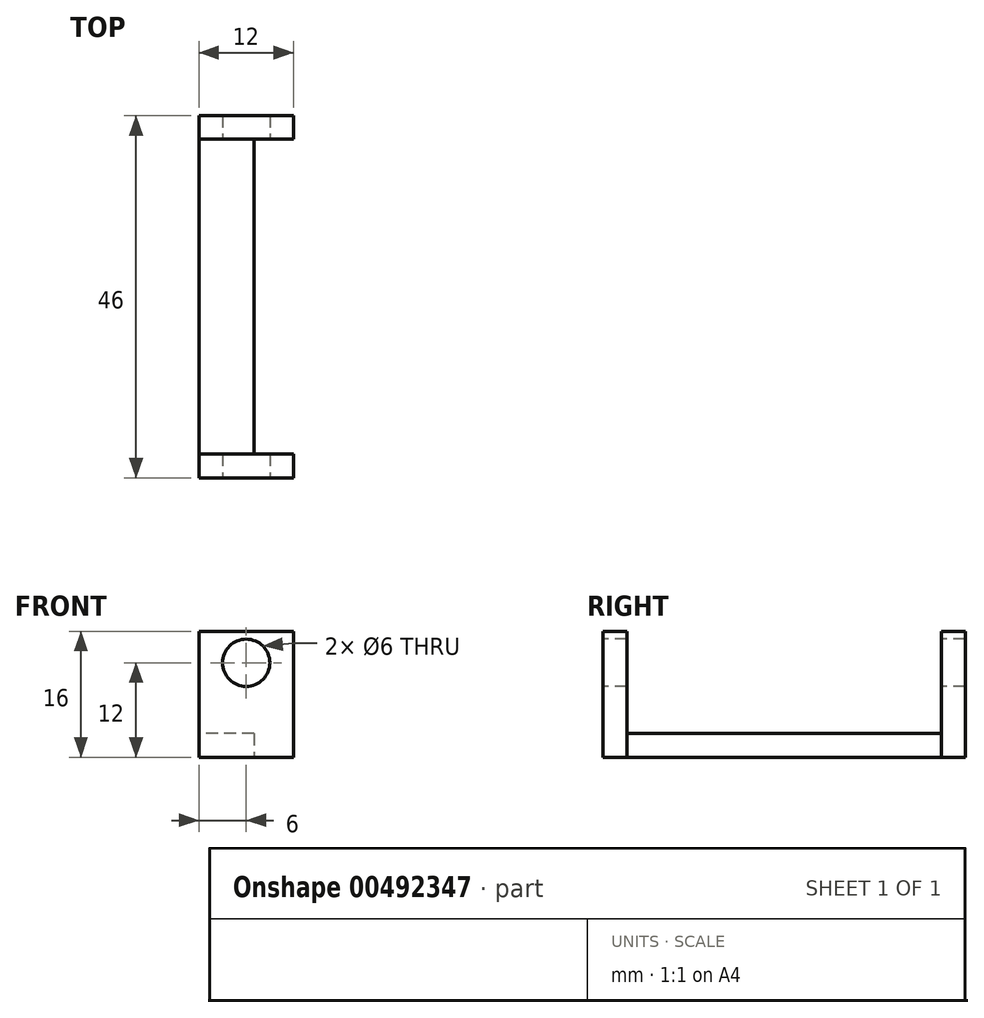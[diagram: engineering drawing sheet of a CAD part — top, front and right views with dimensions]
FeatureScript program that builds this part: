
annotation { "Feature Type Name" : "Feature", "Feature Type Description" : "" }
export const myFeature = defineFeature(function(context is Context, id is Id, definition is map)
    precondition{}
    {
        {
            var Q0;
            Q0=qCreatedBy(makeId("Top.planeOp"),FACE);
            var sketch = newSketch(context, id + "F0", { "sketchPlane" : qUnion([Q0])});
            skLineSegment(sketch, "E0.bottom", {"start": v(-1.5, 20) * mm, "end": v(1.5, 20) * mm});
            skLineSegment(sketch, "E0.top", {"start": v(-1.5, -20) * mm, "end": v(1.5, -20) * mm});
            skLineSegment(sketch, "E0.left", {"start": v(-1.5, 20) * mm, "end": v(-1.5, -20) * mm});
            skLineSegment(sketch, "E0.right", {"start": v(1.5, 20) * mm, "end": v(1.5, -20) * mm});
            skPoint(sketch, "E0.middle", {"position": v(0, 0) * mm});
            skLineSegment(sketch, "E1.bottom", {"start": v(-1.5, 20) * mm, "end": v(10.5, 20) * mm});
            skLineSegment(sketch, "E1.top", {"start": v(-1.5, 23) * mm, "end": v(10.5, 23) * mm});
            skLineSegment(sketch, "E1.left", {"start": v(-1.5, 20) * mm, "end": v(-1.5, 23) * mm});
            skLineSegment(sketch, "E1.right", {"start": v(10.5, 20) * mm, "end": v(10.5, 23) * mm});
            skLineSegment(sketch, "E2.bottom", {"start": v(-1.5, -20) * mm, "end": v(10.5, -20) * mm});
            skLineSegment(sketch, "E2.top", {"start": v(-1.5, -23) * mm, "end": v(10.5, -23) * mm});
            skLineSegment(sketch, "E2.left", {"start": v(-1.5, -20) * mm, "end": v(-1.5, -23) * mm});
            skLineSegment(sketch, "E2.right", {"start": v(10.5, -20) * mm, "end": v(10.5, -23) * mm});
            skSolve(sketch);
        }
        {
            var Q0;
            Q0=makeQuery(id+"F0.imprint","IMPRINT",FACE,{"disambiguationData":[TD([[makeQuery(id+"F0.imprint","IMPRINT",EDGE,{"derivedFrom":sQuery(id+"F0.wireOp",EDGE,"E1.top")}),-1.0]])]});
            var Q1;
            {var subQ0=sQuery(id+"F0.wireOp",EDGE,"E0.left");Q1=makeQuery(id+"F0.imprint","IMPRINT",FACE,{"disambiguationData":[TD([[makeQuery(id+"F0.imprint","IMPRINT",EDGE,{"derivedFrom":subQ0}),1.0]])]});}
            var Q2;
            Q2=makeQuery(id+"F0.imprint","IMPRINT",FACE,{"disambiguationData":[TD([[makeQuery(id+"F0.imprint","IMPRINT",EDGE,{"derivedFrom":sQuery(id+"F0.wireOp",EDGE,"E2.top")}),1.0]])]});
            extrude(context, id + "F1", {"entities" : qUnion([Q0, Q1, Q2]), "depth" : 16 * mm});
        }
        {
            var Q0;
            Q0=makeQuery(id+"F1.opExtrude","SWEPT_FACE",FACE,{"disambiguationData":[OSD([sQuery(id+"F0.wireOp",EDGE,"E2.top")])]});
            var sketch = newSketch(context, id + "F2", { "sketchPlane" : qUnion([Q0])});
            skPoint(sketch, "E3", {"position": v(4.5, 12) * mm});
            skSolve(sketch);
        }
        {
            var Q0;
            Q0=sQuery(id+"F2.wireOp",VERTEX,"E3");
            var Q1;
            Q1=makeQuery(id+"F1.opExtrude","SWEPT_BODY",BODY,{"disambiguationData":[OSD([sQuery(id+"F0.wireOp",EDGE,"E0.left"),sQuery(id+"F0.wireOp",EDGE,"E0.right"),sQuery(id+"F0.wireOp",EDGE,"E1.bottom"),sQuery(id+"F0.wireOp",EDGE,"E1.top"),sQuery(id+"F0.wireOp",EDGE,"E1.left"),sQuery(id+"F0.wireOp",EDGE,"E1.right"),sQuery(id+"F0.wireOp",EDGE,"E2.bottom"),sQuery(id+"F0.wireOp",EDGE,"E2.top"),sQuery(id+"F0.wireOp",EDGE,"E2.left"),sQuery(id+"F0.wireOp",EDGE,"E2.right")])]});
            hole(context, id + "F3", {"style" : HoleStyle.SIMPLE, "endStyle" : HoleEndStyle.THROUGH, "holeDiameter" : 6 * mm, "isTappedThrough" : true, "tappedDepth" : 12 * mm, "tapClearance" : 3, "locations" : qUnion([Q0]), "scope" : qUnion([Q1])});
        }
        {
            var Q0;
            Q0=makeQuery(id+"F1.opExtrude","SWEPT_FACE",FACE,{"disambiguationData":[OSD([sQuery(id+"F0.wireOp",EDGE,"E0.right")])]});
            var sketch = newSketch(context, id + "F4", { "sketchPlane" : qUnion([Q0])});
            skLineSegment(sketch, "E4.bottom", {"start": v(20, 0) * mm, "end": v(-20, 0) * mm});
            skLineSegment(sketch, "E4.top", {"start": v(20, 3) * mm, "end": v(-20, 3) * mm});
            skLineSegment(sketch, "E4.left", {"start": v(20, 0) * mm, "end": v(20, 3) * mm});
            skLineSegment(sketch, "E4.right", {"start": v(-20, 0) * mm, "end": v(-20, 3) * mm});
            skSolve(sketch);
        }
        {
            var Q0;
            Q0=makeQuery(id+"F4.imprint","IMPRINT",FACE,{"disambiguationData":[TD([[makeQuery(id+"F4.imprint","IMPRINT",EDGE,{"derivedFrom":sQuery(id+"F4.wireOp",EDGE,"E4.bottom")}),-1.0]])]});
            extrude(context, id + "F5", {"entities" : qUnion([Q0]), "operationType" : NewBodyOperationType.ADD, "depth" : 4 * mm});
        }
        {
            var Q0;
            Q0=makeQuery(id+"F1.opExtrude","SWEPT_FACE",FACE,{"disambiguationData":[OSD([sQuery(id+"F0.wireOp",EDGE,"E0.right")])]});
            var sketch = newSketch(context, id + "F6", { "sketchPlane" : qUnion([Q0])});
            skLineSegment(sketch, "E5.bottom", {"start": v(-20, 16) * mm, "end": v(20, 16) * mm});
            skLineSegment(sketch, "E5.top", {"start": v(-20, 3) * mm, "end": v(20, 3) * mm});
            skLineSegment(sketch, "E5.left", {"start": v(-20, 16) * mm, "end": v(-20, 3) * mm});
            skLineSegment(sketch, "E5.right", {"start": v(20, 16) * mm, "end": v(20, 3) * mm});
            skSolve(sketch);
        }
        {
            var Q0;
            Q0=makeQuery(id+"F6.imprint","IMPRINT",FACE,{"disambiguationData":[TD([[makeQuery(id+"F6.imprint","IMPRINT",EDGE,{"derivedFrom":sQuery(id+"F6.wireOp",EDGE,"E5.bottom")}),1.0]])]});
            extrude(context, id + "F7", {"entities" : qUnion([Q0]), "operationType" : NewBodyOperationType.REMOVE, "oppositeDirection" : true, "depth" : 25 * mm});
        }
    });
